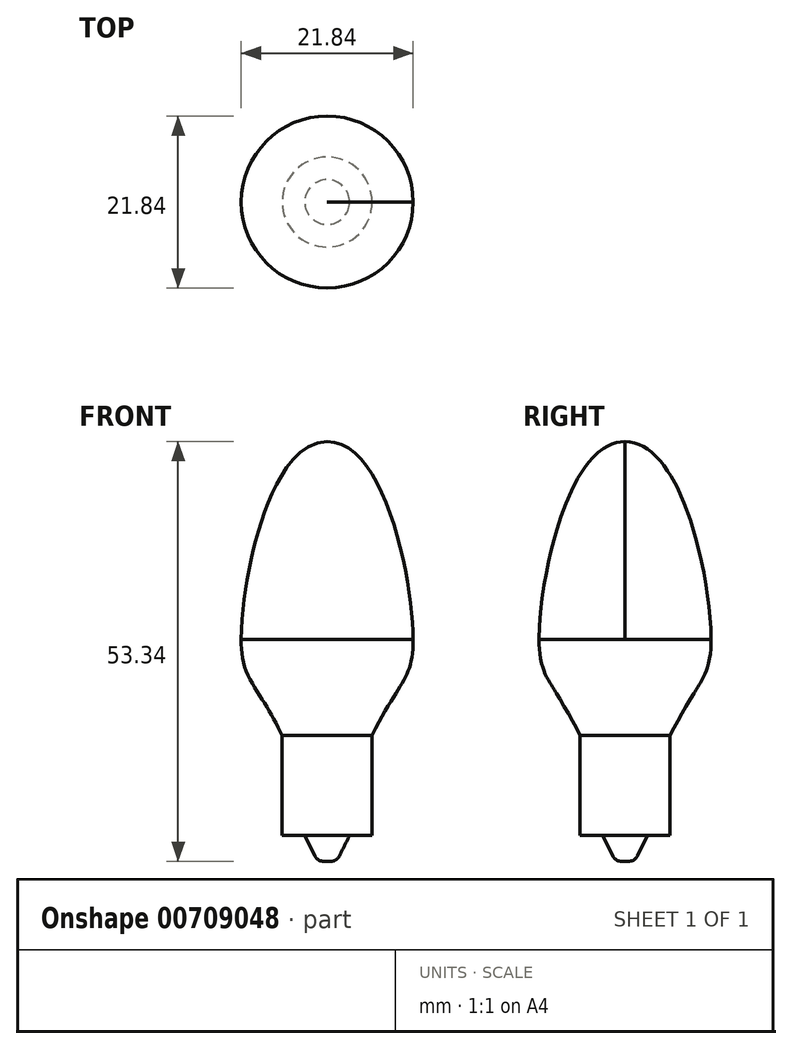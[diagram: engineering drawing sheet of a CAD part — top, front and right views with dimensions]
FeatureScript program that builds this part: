
annotation { "Feature Type Name" : "Feature", "Feature Type Description" : "" }
export const myFeature = defineFeature(function(context is Context, id is Id, definition is map)
    precondition{}
    {
        {
            var Q0;
            Q0=qCreatedBy(makeId("Front.planeOp"),FACE);
            var sketch = newSketch(context, id + "F0", { "sketchPlane" : qUnion([Q0])});
            skLineSegment(sketch, "E0.top", {"start": v(2.84, -12.7) * mm, "end": v(5.72, -12.7) * mm});
            skLineSegment(sketch, "E0.right", {"start": v(5.71, 0) * mm, "end": v(5.72, -12.7) * mm});
            skLineSegment(sketch, "E1.top", {"start": v(0, -16) * mm, "end": v(0.43, -16) * mm});
            skLineSegment(sketch, "E2", {"start": v(2.84, -12.7) * mm, "end": v(1.57, -15.3) * mm});
            skArc(sketch, "E3.filletArc", {"start": v(0.43, -16) * mm, "mid": v(1.1, -15.81) * mm, "end": v(1.57, -15.3) * mm});
            skLineSegment(sketch, "E4.right", {"start": v(10.92, 12.2) * mm, "end": v(10.92, 12.2) * mm});
            skFitSpline(sketch, "E5", {"points": [v(5.72, 0) * mm, v(10.92, 12.2) * mm, v(0, 37.34) * mm], "startDerivative": vector(25.59, 51.56) * mm, "endDerivative": vector(-37.67, 0) * mm});
            skLineSegment(sketch, "E6", {"start": v(0, 37.34) * mm, "end": v(0, -16) * mm});
            skLineSegment(sketch, "E7", {"start": v(5.71, 0) * mm, "end": v(0, 0) * mm});
            skSolve(sketch);
        }
        {
            var Q0;
            Q0=qCreatedBy(makeId("Front.planeOp"),FACE);
            var sketch = newSketch(context, id + "F1", { "sketchPlane" : qUnion([Q0])});
            skLineSegment(sketch, "E8", {"start": v(0, 51.11) * mm, "end": v(0, -26.26) * mm});
            skSolve(sketch);
        }
        {
            var Q0;
            Q0=makeQuery(id+"F0.imprint","IMPRINT",FACE,{"disambiguationData":[TD([[makeQuery(id+"F0.imprint","IMPRINT",EDGE,{"derivedFrom":sQuery(id+"F0.wireOp",EDGE,"E0.top")}),1.0]])]});
            var Q1;
            Q1=sQuery(id+"F1.wireOp",EDGE,"E8");
            revolve(context, id + "F2", {"surfaceOperationType" : NewSurfaceOperationType.NEW, "entities" : qUnion([Q0]), "axis" : qUnion([Q1]), "revolveType" : RevolveType.FULL});
        }
        {
            var Q0;
            Q0=makeQuery(id+"F2.opRevolve","SWEPT_BODY",BODY,{"disambiguationData":[OSD([sQuery(id+"F0.wireOp",EDGE,"E0.top"),sQuery(id+"F0.wireOp",EDGE,"E0.right"),sQuery(id+"F0.wireOp",EDGE,"E1.top"),sQuery(id+"F0.wireOp",EDGE,"E2"),sQuery(id+"F0.wireOp",EDGE,"E3.filletArc"),sQuery(id+"F0.wireOp",EDGE,"E6"),sQuery(id+"F0.wireOp",EDGE,"E7")])]});
            transform(context, id + "F3", {"entities" : qUnion([Q0]), "transformType" : TransformType.TRANSLATION_3D, "dx" : 0 * mm, "dy" : 0 * mm, "dz" : 0 * mm, "makeCopy" : true});
        }
        {
            var Q0;
            Q0=makeQuery(id+"F3.opPattern","COPY",BODY,{"derivedFrom":makeQuery(id+"F2.opRevolve","SWEPT_BODY",BODY,{"disambiguationData":[OSD([sQuery(id+"F0.wireOp",EDGE,"E0.top"),sQuery(id+"F0.wireOp",EDGE,"E0.right"),sQuery(id+"F0.wireOp",EDGE,"E1.top"),sQuery(id+"F0.wireOp",EDGE,"E2"),sQuery(id+"F0.wireOp",EDGE,"E3.filletArc"),sQuery(id+"F0.wireOp",EDGE,"E6"),sQuery(id+"F0.wireOp",EDGE,"E7")])]}),"instanceName":"1"});
            deleteBodies(context, id + "F4", {"entities" : qUnion([Q0])});
        }
        {
            var Q0;
            {var subQ0=sQuery(id+"F0.wireOp",EDGE,"E7");Q0=makeQuery(id+"F0.imprint","IMPRINT",FACE,{"disambiguationData":[TD([[makeQuery(id+"F0.imprint","IMPRINT",EDGE,{"derivedFrom":subQ0}),-1.0]])]});}
            var Q1;
            Q1=sQuery(id+"F1.wireOp",EDGE,"E8");
            revolve(context, id + "F5", {"operationType" : NewBodyOperationType.ADD, "surfaceOperationType" : NewSurfaceOperationType.NEW, "entities" : qUnion([Q0]), "axis" : qUnion([Q1]), "revolveType" : RevolveType.FULL});
        }
        {
            var Q0;
            Q0=makeQuery(id+"F2.opRevolve","SWEPT_BODY",BODY,{"disambiguationData":[OSD([sQuery(id+"F0.wireOp",EDGE,"E0.top"),sQuery(id+"F0.wireOp",EDGE,"E0.right"),sQuery(id+"F0.wireOp",EDGE,"E1.top"),sQuery(id+"F0.wireOp",EDGE,"E2"),sQuery(id+"F0.wireOp",EDGE,"E3.filletArc"),sQuery(id+"F0.wireOp",EDGE,"E6"),sQuery(id+"F0.wireOp",EDGE,"E7")])]});
            transform(context, id + "F6", {"entities" : qUnion([Q0]), "transformType" : TransformType.TRANSLATION_3D, "dx" : 0 * mm, "dy" : 0 * mm, "dz" : 0 * mm, "makeCopy" : true});
        }
        {
            var Q0;
            Q0=makeQuery(id+"F6.opPattern","COPY",BODY,{"derivedFrom":makeQuery(id+"F2.opRevolve","SWEPT_BODY",BODY,{"disambiguationData":[OSD([sQuery(id+"F0.wireOp",EDGE,"E0.top"),sQuery(id+"F0.wireOp",EDGE,"E0.right"),sQuery(id+"F0.wireOp",EDGE,"E1.top"),sQuery(id+"F0.wireOp",EDGE,"E2"),sQuery(id+"F0.wireOp",EDGE,"E3.filletArc"),sQuery(id+"F0.wireOp",EDGE,"E6"),sQuery(id+"F0.wireOp",EDGE,"E7")])]}),"instanceName":"1"});
            deleteBodies(context, id + "F7", {"entities" : qUnion([Q0])});
        }
    });
